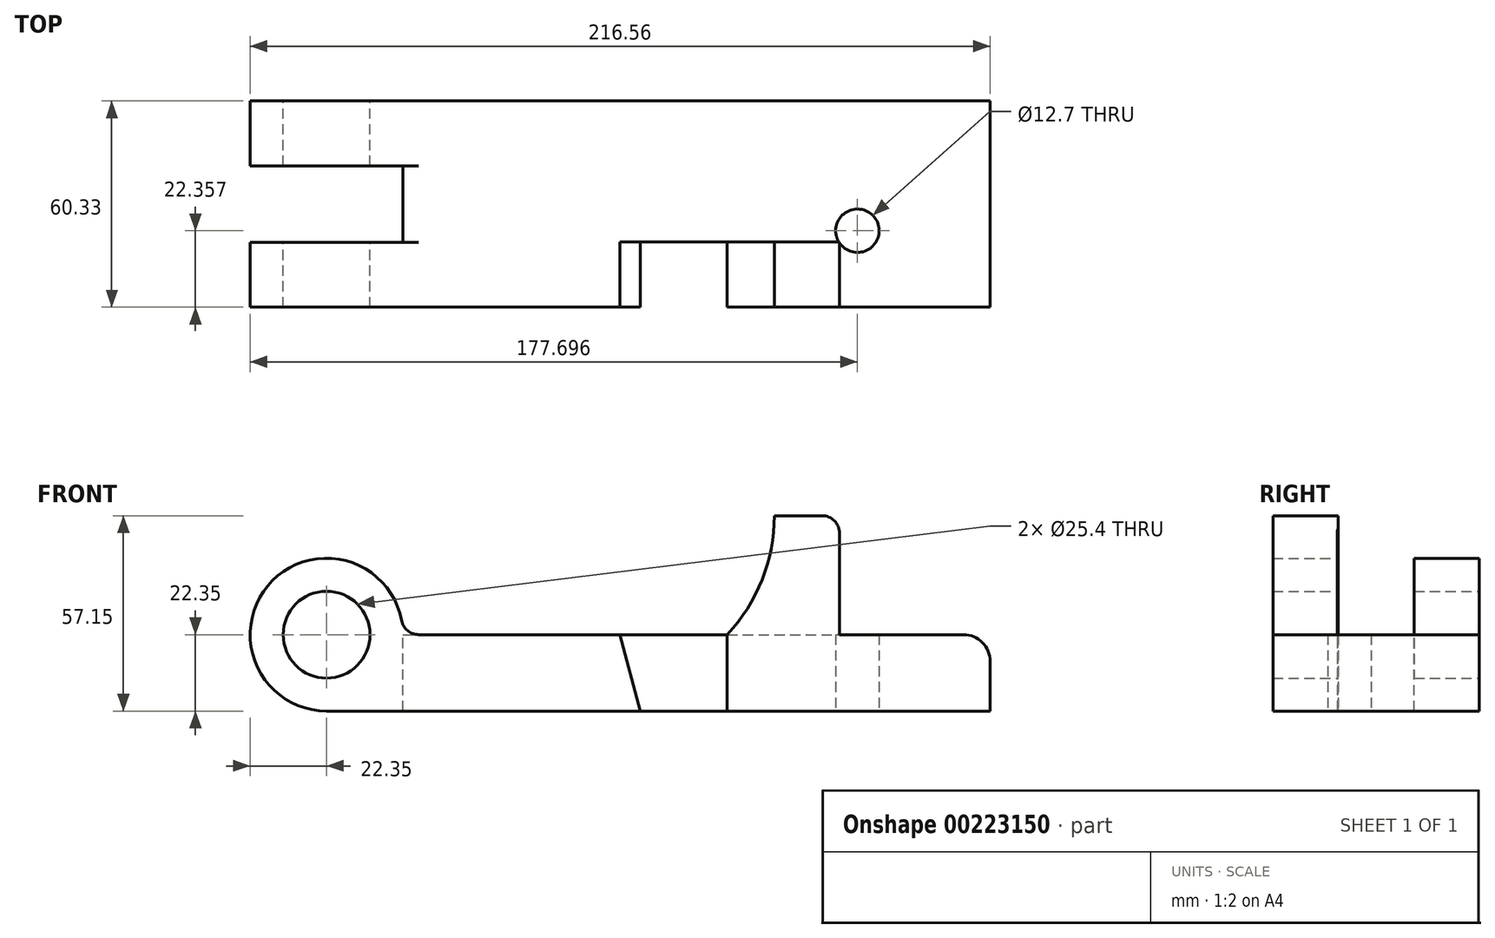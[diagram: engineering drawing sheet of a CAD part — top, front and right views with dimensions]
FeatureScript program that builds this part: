
annotation { "Feature Type Name" : "Feature", "Feature Type Description" : "" }
export const myFeature = defineFeature(function(context is Context, id is Id, definition is map)
    precondition{}
    {
        {
            var Q0;
            Q0=qCreatedBy(makeId("Front.planeOp"),FACE);
            var sketch = newSketch(context, id + "F0", { "sketchPlane" : qUnion([Q0])});
            skCircle(sketch, "E0", {"center": v(0, 0) * mm, "radius": 12.7 * mm});
            skLineSegment(sketch, "E1", {"start": v(0, -22.35) * mm, "end": v(194.2, -22.35) * mm});
            skArc(sketch, "E2", {"start": v(0, -22.35) * mm, "mid": v(-15.8, 15.8) * mm, "end": v(22.35, 0) * mm});
            skLineSegment(sketch, "E3", {"start": v(194.2, -22.35) * mm, "end": v(194.2, 0) * mm});
            skLineSegment(sketch, "E4", {"start": v(22.35, 0) * mm, "end": v(85.85, 0) * mm});
            skLineSegment(sketch, "E5", {"start": v(194.2, 0) * mm, "end": v(150.09, 0) * mm});
            skLineSegment(sketch, "E6", {"start": v(150.09, 0) * mm, "end": v(150.09, 34.8) * mm});
            skLineSegment(sketch, "E7", {"start": v(150.09, 34.8) * mm, "end": v(131.04, 34.8) * mm});
            skLineSegment(sketch, "E8", {"start": v(85.85, 0) * mm, "end": v(117.25, 0) * mm});
            skArc(sketch, "E9", {"start": v(117.25, 0) * mm, "mid": v(127.46, 16.08) * mm, "end": v(131.04, 34.8) * mm});
            skSolve(sketch);
        }
        {
            var Q0;
            Q0 = qSketchRegion(id + "F0", true);
            extrude(context, id + "F1", {"entities" : qUnion([Q0]), "depth" : 60.32 * mm});
        }
        {
            var Q0;
            Q0=makeQuery(id+"F1.opExtrude","CAP_FACE",FACE,{"disambiguationData":[OSD([sQuery(id+"F0.wireOp",EDGE,"E0"),sQuery(id+"F0.wireOp",EDGE,"E1"),sQuery(id+"F0.wireOp",EDGE,"E2"),sQuery(id+"F0.wireOp",EDGE,"E3"),sQuery(id+"F0.wireOp",EDGE,"E4"),sQuery(id+"F0.wireOp",EDGE,"E5"),sQuery(id+"F0.wireOp",EDGE,"E6"),sQuery(id+"F0.wireOp",EDGE,"E7"),sQuery(id+"F0.wireOp",EDGE,"E8"),sQuery(id+"F0.wireOp",EDGE,"E9")])],"isStart":false});
            var sketch = newSketch(context, id + "F2", { "sketchPlane" : qUnion([Q0])});
            skLineSegment(sketch, "E10", {"start": v(85.85, 0) * mm, "end": v(91.85, -22.35) * mm});
            skLineSegment(sketch, "E11", {"start": v(117.25, -22.35) * mm, "end": v(117.25, 0) * mm});
            skLineSegment(sketch, "E12", {"start": v(85.85, 0) * mm, "end": v(117.25, 0) * mm});
            skLineSegment(sketch, "E13", {"start": v(91.85, -22.35) * mm, "end": v(117.25, -22.35) * mm});
            skSolve(sketch);
        }
        {
            var Q0;
            Q0 = qSketchRegion(id + "F2", true);
            extrude(context, id + "F3", {"entities" : qUnion([Q0]), "operationType" : NewBodyOperationType.REMOVE, "oppositeDirection" : true, "depth" : 19.05 * mm});
        }
        {
            var Q0;
            Q0=makeQuery(id+"F1.opExtrude","CAP_FACE",FACE,{"disambiguationData":[OSD([sQuery(id+"F0.wireOp",EDGE,"E0"),sQuery(id+"F0.wireOp",EDGE,"E1"),sQuery(id+"F0.wireOp",EDGE,"E2"),sQuery(id+"F0.wireOp",EDGE,"E3"),sQuery(id+"F0.wireOp",EDGE,"E4"),sQuery(id+"F0.wireOp",EDGE,"E5"),sQuery(id+"F0.wireOp",EDGE,"E6"),sQuery(id+"F0.wireOp",EDGE,"E7"),sQuery(id+"F0.wireOp",EDGE,"E8"),sQuery(id+"F0.wireOp",EDGE,"E9")])],"isStart":true});
            var sketch = newSketch(context, id + "F4", { "sketchPlane" : qUnion([Q0])});
            skLineSegment(sketch, "E14", {"start": v(-150.09, 0) * mm, "end": v(-150.09, 34.8) * mm});
            skLineSegment(sketch, "E15", {"start": v(-150.09, 34.8) * mm, "end": v(-131.04, 34.8) * mm});
            skLineSegment(sketch, "E16", {"start": v(-117.25, 0) * mm, "end": v(-150.09, 0) * mm});
            skArc(sketch, "E17", {"start": v(-131.04, 34.8) * mm, "mid": v(-127.46, 16.08) * mm, "end": v(-117.25, 0) * mm});
            skSolve(sketch);
        }
        {
            var Q0;
            Q0 = qSketchRegion(id + "F4", true);
            extrude(context, id + "F5", {"entities" : qUnion([Q0]), "operationType" : NewBodyOperationType.REMOVE, "oppositeDirection" : true, "depth" : 41.27 * mm});
        }
        {
            var Q0;
            Q0=makeQuery(id+"F1.opExtrude","SWEPT_FACE",FACE,{"disambiguationData":[OSD([sQuery(id+"F0.wireOp",EDGE,"E1")])]});
            var sketch = newSketch(context, id + "F6", { "sketchPlane" : qUnion([Q0])});
            skCircle(sketch, "E18", {"center": v(155.35, 37.97) * mm, "radius": 6.35 * mm});
            skSolve(sketch);
        }
        {
            var Q0;
            Q0 = qSketchRegion(id + "F6", true);
            extrude(context, id + "F7", {"entities" : qUnion([Q0]), "operationType" : NewBodyOperationType.REMOVE, "endBound" : BoundingType.UP_TO_NEXT, "oppositeDirection" : true, "depth" : 25.4 * mm});
        }
        {
            var Q0;
            Q0=makeQuery(id+"F5.boolean.opBoolean","MERGE",FACE,{"derivedFrom":[makeQuery(id+"F1.opExtrude","SWEPT_FACE",FACE,{"disambiguationData":[OSD([sQuery(id+"F0.wireOp",EDGE,"E5")])]}),makeQuery(id+"F1.opExtrude","SWEPT_FACE",FACE,{"disambiguationData":[OSD([sQuery(id+"F0.wireOp",EDGE,"E4"),sQuery(id+"F0.wireOp",EDGE,"E8")])]}),makeQuery(id+"F5.opExtrude","SWEPT_FACE",FACE,{"disambiguationData":[OSD([sQuery(id+"F4.wireOp",EDGE,"E16")])]})]});
            var sketch = newSketch(context, id + "F8", { "sketchPlane" : qUnion([Q0])});
            skLineSegment(sketch, "E19", {"start": v(22.35, -19) * mm, "end": v(-35.33, -19) * mm});
            skLineSegment(sketch, "E20", {"start": v(-35.33, -19) * mm, "end": v(-35.33, -41.33) * mm});
            skLineSegment(sketch, "E21", {"start": v(-35.33, -41.33) * mm, "end": v(22.35, -41.33) * mm});
            skLineSegment(sketch, "E22", {"start": v(22.35, -19) * mm, "end": v(22.35, -41.33) * mm});
            skSolve(sketch);
        }
        {
            var Q0;
            Q0 = qSketchRegion(id + "F8", true);
            extrude(context, id + "F9", {"entities" : qUnion([Q0]), "operationType" : NewBodyOperationType.REMOVE, "endBound" : BoundingType.SYMMETRIC, "oppositeDirection" : true, "depth" : 50.8 * mm});
        }
        {
            var Q0;
            Q0=makeQuery(id+"F1.opExtrude","SWEPT_EDGE",EDGE,{"disambiguationData":[OSD([sQuery(id+"F0.wireOp",EDGE,"E3"),sQuery(id+"F0.wireOp",EDGE,"E5")])]});
            fillet(context, id + "F10", {"entities" : qUnion([Q0]), "radius" : 7.87 * mm, "tangentPropagation" : true, "allowEdgeOverflow" : false});
        }
        {
            var Q0;
            Q0=makeQuery(id+"F1.opExtrude","SWEPT_EDGE",EDGE,{"disambiguationData":[OSD([sQuery(id+"F0.wireOp",EDGE,"E6"),sQuery(id+"F0.wireOp",EDGE,"E7")])]});
            fillet(context, id + "F11", {"entities" : qUnion([Q0]), "radius" : 5.08 * mm, "tangentPropagation" : true, "allowEdgeOverflow" : false});
        }
        {
            var Q0;
            {var subQ0=sQuery(id+"F0.wireOp",EDGE,"E5");var subQ1=sQuery(id+"F0.wireOp",EDGE,"E8");var subQ2=sQuery(id+"F0.wireOp",EDGE,"E4");var subQ3=sQuery(id+"F0.wireOp",EDGE,"E2");Q0=makeQuery(id+"F9.boolean.opBoolean","SPLIT",EDGE,{"disambiguationData":[TD([makeQuery(id+"F1.opExtrude","CAP_FACE",FACE,{"disambiguationData":[OSD([sQuery(id+"F0.wireOp",EDGE,"E0"),sQuery(id+"F0.wireOp",EDGE,"E1"),subQ3,sQuery(id+"F0.wireOp",EDGE,"E3"),subQ2,subQ0,sQuery(id+"F0.wireOp",EDGE,"E6"),sQuery(id+"F0.wireOp",EDGE,"E7"),subQ1,sQuery(id+"F0.wireOp",EDGE,"E9")])],"isStart":true}),makeQuery(id+"F1.opExtrude","SWEPT_FACE",FACE,{"disambiguationData":[OSD([subQ3])]}),makeQuery(id+"F1.opExtrude","SWEPT_FACE",FACE,{"disambiguationData":[OSD([subQ2,subQ1])]}),makeQuery(id+"F1.opExtrude","SWEPT_FACE",FACE,{"disambiguationData":[OSD([subQ0])]}),makeQuery(id+"F5.opExtrude","SWEPT_FACE",FACE,{"disambiguationData":[OSD([sQuery(id+"F4.wireOp",EDGE,"E16")])]}),makeQuery(id+"F9.opExtrude","SWEPT_FACE",FACE,{"disambiguationData":[OSD([sQuery(id+"F8.wireOp",EDGE,"E19")])]}),makeQuery(id+"F9.opExtrude","SWEPT_FACE",FACE,{"disambiguationData":[OSD([sQuery(id+"F8.wireOp",EDGE,"E22")])]})])],"derivedFrom":makeQuery(id+"F1.opExtrude","SWEPT_EDGE",EDGE,{"disambiguationData":[OSD([subQ3,subQ2])]})});}
            var Q1;
            {var subQ0=sQuery(id+"F0.wireOp",EDGE,"E5");var subQ1=sQuery(id+"F0.wireOp",EDGE,"E8");var subQ2=sQuery(id+"F0.wireOp",EDGE,"E4");var subQ3=sQuery(id+"F0.wireOp",EDGE,"E2");Q1=makeQuery(id+"F9.boolean.opBoolean","SPLIT",EDGE,{"disambiguationData":[TD([makeQuery(id+"F1.opExtrude","CAP_FACE",FACE,{"disambiguationData":[OSD([sQuery(id+"F0.wireOp",EDGE,"E0"),sQuery(id+"F0.wireOp",EDGE,"E1"),subQ3,sQuery(id+"F0.wireOp",EDGE,"E3"),subQ2,subQ0,sQuery(id+"F0.wireOp",EDGE,"E6"),sQuery(id+"F0.wireOp",EDGE,"E7"),subQ1,sQuery(id+"F0.wireOp",EDGE,"E9")])],"isStart":false}),makeQuery(id+"F1.opExtrude","SWEPT_FACE",FACE,{"disambiguationData":[OSD([subQ3])]}),makeQuery(id+"F1.opExtrude","SWEPT_FACE",FACE,{"disambiguationData":[OSD([subQ2,subQ1])]}),makeQuery(id+"F1.opExtrude","SWEPT_FACE",FACE,{"disambiguationData":[OSD([subQ0])]}),makeQuery(id+"F5.opExtrude","SWEPT_FACE",FACE,{"disambiguationData":[OSD([sQuery(id+"F4.wireOp",EDGE,"E16")])]}),makeQuery(id+"F9.opExtrude","SWEPT_FACE",FACE,{"disambiguationData":[OSD([sQuery(id+"F8.wireOp",EDGE,"E21")])]}),makeQuery(id+"F9.opExtrude","SWEPT_FACE",FACE,{"disambiguationData":[OSD([sQuery(id+"F8.wireOp",EDGE,"E22")])]})])],"derivedFrom":makeQuery(id+"F1.opExtrude","SWEPT_EDGE",EDGE,{"disambiguationData":[OSD([subQ3,subQ2])]})});}
            fillet(context, id + "F12", {"entities" : qUnion([Q0, Q1]), "radius" : 5.08 * mm, "tangentPropagation" : true, "allowEdgeOverflow" : false});
        }
    });
